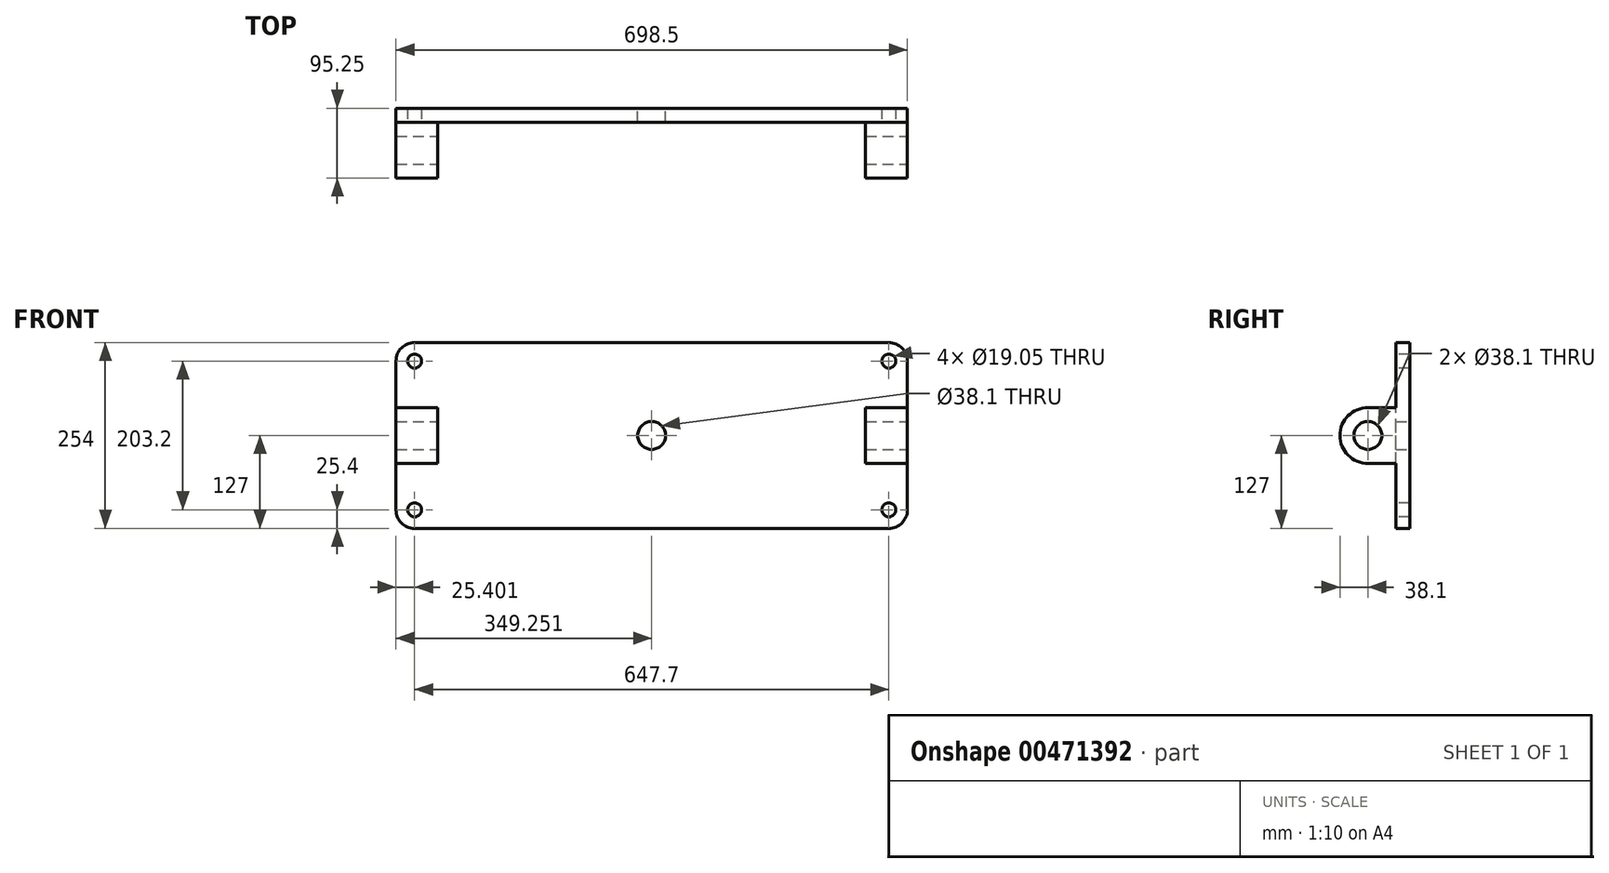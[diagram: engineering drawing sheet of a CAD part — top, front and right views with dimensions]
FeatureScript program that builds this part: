
annotation { "Feature Type Name" : "Feature", "Feature Type Description" : "" }
export const myFeature = defineFeature(function(context is Context, id is Id, definition is map)
    precondition{}
    {
        {
            var Q0;
            Q0=qCreatedBy(makeId("Front.planeOp"),FACE);
            var sketch = newSketch(context, id + "F0", { "sketchPlane" : qUnion([Q0])});
            skLineSegment(sketch, "E0", {"start": v(-304.5, 0) * mm, "end": v(394, 0) * mm});
            skLineSegment(sketch, "E1", {"start": v(-304.5, 0) * mm, "end": v(-304.5, 254) * mm});
            skLineSegment(sketch, "E2", {"start": v(-304.5, 254) * mm, "end": v(394, 254) * mm});
            skLineSegment(sketch, "E3", {"start": v(394, 254) * mm, "end": v(394, 0) * mm});
            skLineSegment(sketch, "E4", {"start": v(44.75, 0) * mm, "end": v(44.75, 127) * mm});
            skCircle(sketch, "E5", {"center": v(44.75, 127) * mm, "radius": 19.05 * mm});
            skSolve(sketch);
        }
        {
            var Q0;
            {var subQ0=sQuery(id+"F0.wireOp",EDGE,"E1");Q0=makeQuery(id+"F0.imprint","IMPRINT",FACE,{"disambiguationData":[TD([[makeQuery(id+"F0.imprint","IMPRINT",EDGE,{"derivedFrom":subQ0}),-1.0]])]});}
            extrude(context, id + "F1", {"entities" : qUnion([Q0]), "depth" : 19.05 * mm});
        }
        {
            var Q0;
            Q0=makeQuery(id+"F1.opExtrude","SWEPT_EDGE",EDGE,{"disambiguationData":[OSD([sQuery(id+"F0.wireOp",EDGE,"E1"),sQuery(id+"F0.wireOp",EDGE,"E2")])]});
            var Q1;
            Q1=makeQuery(id+"F1.opExtrude","SWEPT_EDGE",EDGE,{"disambiguationData":[OSD([sQuery(id+"F0.wireOp",EDGE,"E2"),sQuery(id+"F0.wireOp",EDGE,"E3")])]});
            var Q2;
            Q2=makeQuery(id+"F1.opExtrude","SWEPT_EDGE",EDGE,{"disambiguationData":[OSD([sQuery(id+"F0.wireOp",EDGE,"E0"),sQuery(id+"F0.wireOp",EDGE,"E3")])]});
            var Q3;
            Q3=makeQuery(id+"F1.opExtrude","SWEPT_EDGE",EDGE,{"disambiguationData":[OSD([sQuery(id+"F0.wireOp",EDGE,"E0"),sQuery(id+"F0.wireOp",EDGE,"E1")])]});
            fillet(context, id + "F2", {"entities" : qUnion([Q0, Q1, Q2, Q3]), "radius" : 25.4 * mm, "tangentPropagation" : true, "allowEdgeOverflow" : false});
        }
        {
            var Q0;
            Q0=makeQuery(id+"F1.opExtrude","CAP_FACE",FACE,{"disambiguationData":[OSD([sQuery(id+"F0.wireOp",EDGE,"E0"),sQuery(id+"F0.wireOp",EDGE,"E1"),sQuery(id+"F0.wireOp",EDGE,"E2"),sQuery(id+"F0.wireOp",EDGE,"E3"),sQuery(id+"F0.wireOp",EDGE,"E5")])],"isStart":false});
            var sketch = newSketch(context, id + "F3", { "sketchPlane" : qUnion([Q0])});
            skCircle(sketch, "E6", {"center": v(-279.1, 228.6) * mm, "radius": 9.53 * mm});
            skCircle(sketch, "E7", {"center": v(-279.1, 25.4) * mm, "radius": 9.53 * mm});
            skCircle(sketch, "E8", {"center": v(368.6, 228.6) * mm, "radius": 9.53 * mm});
            skCircle(sketch, "E9", {"center": v(368.6, 25.4) * mm, "radius": 9.53 * mm});
            skSolve(sketch);
        }
        {
            var Q0;
            Q0=makeQuery(id+"F1.opExtrude","CAP_FACE",FACE,{"disambiguationData":[OSD([sQuery(id+"F0.wireOp",EDGE,"E0"),sQuery(id+"F0.wireOp",EDGE,"E1"),sQuery(id+"F0.wireOp",EDGE,"E2"),sQuery(id+"F0.wireOp",EDGE,"E3"),sQuery(id+"F0.wireOp",EDGE,"E5")])],"isStart":false});
            var sketch = newSketch(context, id + "F4", { "sketchPlane" : qUnion([Q0])});
            skLineSegment(sketch, "E10.bottom", {"start": v(-304.5, 127) * mm, "end": v(-247.35, 127) * mm});
            skLineSegment(sketch, "E10.top", {"start": v(-304.5, 88.9) * mm, "end": v(-247.35, 88.9) * mm});
            skLineSegment(sketch, "E10.left", {"start": v(-304.5, 127) * mm, "end": v(-304.5, 88.9) * mm});
            skLineSegment(sketch, "E10.right", {"start": v(-247.35, 127) * mm, "end": v(-247.35, 88.9) * mm});
            skLineSegment(sketch, "E11.top", {"start": v(-304.5, 165.1) * mm, "end": v(-247.35, 165.1) * mm});
            skLineSegment(sketch, "E11.left", {"start": v(-304.5, 127) * mm, "end": v(-304.5, 165.1) * mm});
            skLineSegment(sketch, "E11.right", {"start": v(-247.35, 127) * mm, "end": v(-247.35, 165.1) * mm});
            skLineSegment(sketch, "E12", {"start": v(394, 88.9) * mm, "end": v(394, 165.1) * mm});
            skLineSegment(sketch, "E13", {"start": v(394, 165.1) * mm, "end": v(336.85, 165.1) * mm});
            skLineSegment(sketch, "E14", {"start": v(336.85, 88.9) * mm, "end": v(394, 88.9) * mm});
            skLineSegment(sketch, "E15", {"start": v(336.85, 165.1) * mm, "end": v(336.85, 88.9) * mm});
            skLineSegment(sketch, "E16", {"start": v(336.85, 127) * mm, "end": v(394, 127) * mm});
            skSolve(sketch);
        }
        {
            var Q0;
            Q0=makeQuery(id+"F4.imprint","IMPRINT",FACE,{"disambiguationData":[TD([[makeQuery(id+"F4.imprint","IMPRINT",EDGE,{"derivedFrom":sQuery(id+"F4.wireOp",EDGE,"E10.bottom")}),1.0]])]});
            var Q1;
            Q1=makeQuery(id+"F4.imprint","IMPRINT",FACE,{"disambiguationData":[TD([[makeQuery(id+"F4.imprint","IMPRINT",EDGE,{"derivedFrom":sQuery(id+"F4.wireOp",EDGE,"E10.top")}),1.0]])]});
            extrude(context, id + "F5", {"entities" : qUnion([Q0, Q1]), "operationType" : NewBodyOperationType.ADD, "depth" : 38.1 * mm});
        }
        {
            var Q0;
            Q0=makeQuery(id+"F5.boolean.opBoolean","MERGE",FACE,{"derivedFrom":[makeQuery(id+"F1.opExtrude","SWEPT_FACE",FACE,{"disambiguationData":[OSD([sQuery(id+"F0.wireOp",EDGE,"E1")])]}),makeQuery(id+"F5.opExtrude","SWEPT_FACE",FACE,{"disambiguationData":[OSD([sQuery(id+"F4.wireOp",EDGE,"E10.left"),sQuery(id+"F4.wireOp",EDGE,"E11.left")])]})]});
            var sketch = newSketch(context, id + "F6", { "sketchPlane" : qUnion([Q0])});
            skCircle(sketch, "E17", {"center": v(57.15, 127) * mm, "radius": 38.1 * mm});
            skSolve(sketch);
        }
        {
            var Q0;
            {var subQ1=sQuery(id+"F4.wireOp",EDGE,"E11.left");var subQ2=sQuery(id+"F4.wireOp",EDGE,"E10.left");var subQ3=makeQuery(id+"F5.opExtrude","CAP_EDGE",EDGE,{"disambiguationData":[OSD([subQ2,subQ1])],"isStart":false});Q0=makeQuery(id+"F6.imprint","IMPRINT",FACE,{"disambiguationData":[TD([[makeQuery(id+"F6.imprint","IMPRINT",EDGE,{"derivedFrom":subQ3}),-1.0]])]});}
            extrude(context, id + "F7", {"entities" : qUnion([Q0]), "operationType" : NewBodyOperationType.ADD, "oppositeDirection" : true, "depth" : 57.15 * mm});
        }
        {
            var Q0;
            Q0=makeQuery(id+"F7.boolean.opBoolean","MERGE",FACE,{"derivedFrom":[makeQuery(id+"F5.opExtrude","SWEPT_FACE",FACE,{"disambiguationData":[OSD([sQuery(id+"F4.wireOp",EDGE,"E10.right"),sQuery(id+"F4.wireOp",EDGE,"E11.right")])]}),makeQuery(id+"F7.opExtrude","CAP_FACE",FACE,{"disambiguationData":[OSD([sQuery(id+"F4.wireOp",EDGE,"E10.left"),sQuery(id+"F4.wireOp",EDGE,"E11.left"),sQuery(id+"F6.wireOp",EDGE,"E17")])],"isStart":false})]});
            var sketch = newSketch(context, id + "F8", { "sketchPlane" : qUnion([Q0])});
            skCircle(sketch, "E18", {"center": v(-57.15, 127) * mm, "radius": 19.05 * mm});
            skSolve(sketch);
        }
        {
            var Q0;
            Q0=makeQuery(id+"F1.opExtrude","CAP_FACE",FACE,{"disambiguationData":[OSD([sQuery(id+"F0.wireOp",EDGE,"E0"),sQuery(id+"F0.wireOp",EDGE,"E1"),sQuery(id+"F0.wireOp",EDGE,"E2"),sQuery(id+"F0.wireOp",EDGE,"E3"),sQuery(id+"F0.wireOp",EDGE,"E5")])],"isStart":false});
            var sketch = newSketch(context, id + "F9", { "sketchPlane" : qUnion([Q0])});
            skSolve(sketch);
        }
        {
            var Q0;
            Q0=makeQuery(id+"F8.imprint","IMPRINT",FACE,{"disambiguationData":[TD([[makeQuery(id+"F8.imprint","IMPRINT",EDGE,{"derivedFrom":sQuery(id+"F8.wireOp",EDGE,"E18")}),1.0]])]});
            extrude(context, id + "F10", {"entities" : qUnion([Q0]), "operationType" : NewBodyOperationType.REMOVE, "oppositeDirection" : true, "depth" : 76.2 * mm});
        }
        {
            var Q0;
            Q0=makeQuery(id+"F3.imprint","IMPRINT",FACE,{"disambiguationData":[TD([[makeQuery(id+"F3.imprint","IMPRINT",EDGE,{"derivedFrom":sQuery(id+"F3.wireOp",EDGE,"E6")}),-1.0]])]});
            var sketch = newSketch(context, id + "F11", { "sketchPlane" : qUnion([Q0])});
            skSolve(sketch);
        }
        {
            var Q0;
            Q0 = qSketchRegion(id + "F4", true);
            extrude(context, id + "F12", {"entities" : qUnion([Q0]), "operationType" : NewBodyOperationType.ADD, "depth" : 38.1 * mm});
        }
        {
            var Q0;
            Q0=makeQuery(id+"F12.boolean.opBoolean","MERGE",FACE,{"derivedFrom":[makeQuery(id+"F1.opExtrude","SWEPT_FACE",FACE,{"disambiguationData":[OSD([sQuery(id+"F0.wireOp",EDGE,"E3")])]}),makeQuery(id+"F12.opExtrude","SWEPT_FACE",FACE,{"disambiguationData":[OSD([sQuery(id+"F4.wireOp",EDGE,"E12")])]})]});
            var sketch = newSketch(context, id + "F13", { "sketchPlane" : qUnion([Q0])});
            skCircle(sketch, "E19", {"center": v(-57.15, 127) * mm, "radius": 38.1 * mm});
            skSolve(sketch);
        }
        {
            var Q0;
            {var subQ1=sQuery(id+"F4.wireOp",EDGE,"E12");var subQ2=makeQuery(id+"F12.opExtrude","CAP_EDGE",EDGE,{"disambiguationData":[OSD([subQ1])],"isStart":false});Q0=makeQuery(id+"F13.imprint","IMPRINT",FACE,{"disambiguationData":[TD([[makeQuery(id+"F13.imprint","IMPRINT",EDGE,{"derivedFrom":subQ2}),-1.0]])]});}
            extrude(context, id + "F14", {"entities" : qUnion([Q0]), "operationType" : NewBodyOperationType.ADD, "oppositeDirection" : true, "depth" : 57.15 * mm});
        }
        {
            var Q0;
            {var subQ0=sQuery(id+"F4.wireOp",EDGE,"E12");Q0=makeQuery(id+"F14.boolean.opBoolean","MERGE",FACE,{"derivedFrom":[makeQuery(id+"F12.boolean.opBoolean","MERGE",FACE,{"derivedFrom":[makeQuery(id+"F1.opExtrude","SWEPT_FACE",FACE,{"disambiguationData":[OSD([sQuery(id+"F0.wireOp",EDGE,"E3")])]}),makeQuery(id+"F12.opExtrude","SWEPT_FACE",FACE,{"disambiguationData":[OSD([subQ0])]})]}),makeQuery(id+"F14.opExtrude","CAP_FACE",FACE,{"disambiguationData":[OSD([subQ0,sQuery(id+"F13.wireOp",EDGE,"E19")])],"isStart":true})]});}
            var sketch = newSketch(context, id + "F15", { "sketchPlane" : qUnion([Q0])});
            skCircle(sketch, "E20", {"center": v(-57.15, 127) * mm, "radius": 19.05 * mm});
            skSolve(sketch);
        }
        {
            var Q0;
            Q0=makeQuery(id+"F8.imprint","IMPRINT",FACE,{"disambiguationData":[TD([[makeQuery(id+"F8.imprint","IMPRINT",EDGE,{"derivedFrom":sQuery(id+"F8.wireOp",EDGE,"E18")}),1.0]])]});
            extrude(context, id + "F16", {"entities" : qUnion([Q0]), "operationType" : NewBodyOperationType.REMOVE, "oppositeDirection" : true, "depth" : 76.2 * mm});
        }
        {
            var Q0;
            Q0=makeQuery(id+"F15.imprint","IMPRINT",FACE,{"disambiguationData":[TD([[makeQuery(id+"F15.imprint","IMPRINT",EDGE,{"derivedFrom":sQuery(id+"F15.wireOp",EDGE,"E20")}),1.0]])]});
            extrude(context, id + "F17", {"entities" : qUnion([Q0]), "operationType" : NewBodyOperationType.REMOVE, "oppositeDirection" : true, "depth" : 57.15 * mm});
        }
        {
            var Q0;
            Q0=makeQuery(id+"F11.imprint","IMPRINT",FACE,{"disambiguationData":[TD([[makeQuery(id+"F11.imprint","IMPRINT",EDGE,{"derivedFrom":makeQuery(id+"F3.imprint","IMPRINT",EDGE,{"derivedFrom":sQuery(id+"F3.wireOp",EDGE,"E6")})}),1.0]])]});
            var Q1;
            Q1=makeQuery(id+"F11.imprint","IMPRINT",FACE,{"disambiguationData":[TD([[makeQuery(id+"F11.imprint","IMPRINT",EDGE,{"derivedFrom":makeQuery(id+"F3.imprint","IMPRINT",EDGE,{"derivedFrom":sQuery(id+"F3.wireOp",EDGE,"E7")})}),1.0]])]});
            var Q2;
            Q2=makeQuery(id+"F11.imprint","IMPRINT",FACE,{"disambiguationData":[TD([[makeQuery(id+"F11.imprint","IMPRINT",EDGE,{"derivedFrom":makeQuery(id+"F3.imprint","IMPRINT",EDGE,{"derivedFrom":sQuery(id+"F3.wireOp",EDGE,"E8")})}),1.0]])]});
            var Q3;
            Q3=makeQuery(id+"F11.imprint","IMPRINT",FACE,{"disambiguationData":[TD([[makeQuery(id+"F11.imprint","IMPRINT",EDGE,{"derivedFrom":makeQuery(id+"F3.imprint","IMPRINT",EDGE,{"derivedFrom":sQuery(id+"F3.wireOp",EDGE,"E9")})}),1.0]])]});
            extrude(context, id + "F18", {"entities" : qUnion([Q0, Q1, Q2, Q3]), "operationType" : NewBodyOperationType.REMOVE, "oppositeDirection" : true, "depth" : 25.4 * mm});
        }
    });
